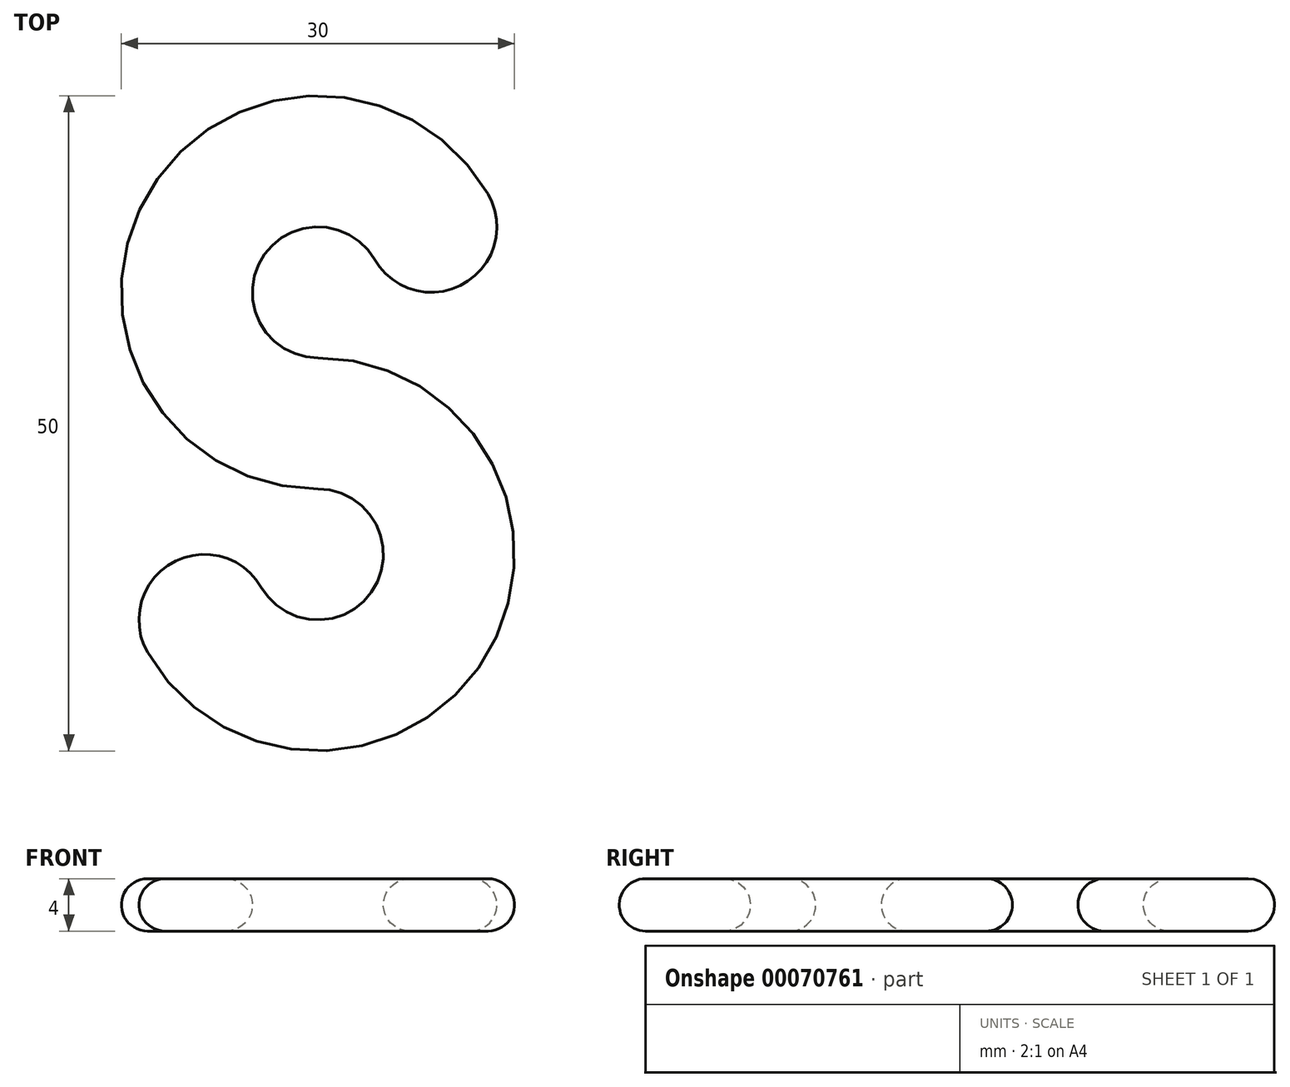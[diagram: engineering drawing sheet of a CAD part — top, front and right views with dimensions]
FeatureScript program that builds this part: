
annotation { "Feature Type Name" : "Feature", "Feature Type Description" : "" }
export const myFeature = defineFeature(function(context is Context, id is Id, definition is map)
    precondition{}
    {
        {
            var Q0;
            Q0=qCreatedBy(makeId("Top.planeOp"),FACE);
            var sketch = newSketch(context, id + "F0", { "sketchPlane" : qUnion([Q0])});
            skCircle(sketch, "E0", {"center": v(0, 0) * mm, "radius": 15 * mm});
            skCircle(sketch, "E1", {"center": v(0, 0) * mm, "radius": 5 * mm});
            skCircle(sketch, "E2", {"center": v(-8.66, -5) * mm, "radius": 5 * mm});
            skCircle(sketch, "E3", {"center": v(0, 20) * mm, "radius": 15 * mm});
            skCircle(sketch, "E4", {"center": v(0, 20) * mm, "radius": 5 * mm});
            skCircle(sketch, "E5", {"center": v(8.66, 25) * mm, "radius": 5 * mm});
            skSolve(sketch);
        }
        {
            var Q0;
            {var subQ0=sQuery(id+"F0.wireOp",EDGE,"E3");var subQ1=sQuery(id+"F0.wireOp",EDGE,"E0");var subQ2=makeQuery(id+"F0.imprint","INTERSECT",VERTEX,{"disambiguationData":[OD(1.0)],"derivedFrom":[subQ1,subQ0]});Q0=makeQuery(id+"F0.imprint","IMPRINT",FACE,{"disambiguationData":[TD([[makeQuery(id+"F0.imprint","IMPRINT",EDGE,{"disambiguationData":[TD([[subQ2,1.0]])],"derivedFrom":subQ1}),-1.0]])]});}
            var Q1;
            {var subQ0=sQuery(id+"F0.wireOp",EDGE,"E5");var subQ1=makeQuery(id+"F0.imprint","INTERSECT",VERTEX,{"derivedFrom":[sQuery(id+"F0.wireOp",EDGE,"E3"),subQ0]});Q1=makeQuery(id+"F0.imprint","IMPRINT",FACE,{"disambiguationData":[TD([[makeQuery(id+"F0.imprint","IMPRINT",EDGE,{"disambiguationData":[TD([[subQ1,-1.0]])],"derivedFrom":subQ0}),1.0]])]});}
            var Q2;
            {var subQ0=sQuery(id+"F0.wireOp",EDGE,"E3");var subQ1=sQuery(id+"F0.wireOp",EDGE,"E0");var subQ2=makeQuery(id+"F0.imprint","INTERSECT",VERTEX,{"disambiguationData":[OD(0.0)],"derivedFrom":[subQ1,subQ0]});Q2=makeQuery(id+"F0.imprint","IMPRINT",FACE,{"disambiguationData":[TD([[makeQuery(id+"F0.imprint","IMPRINT",EDGE,{"disambiguationData":[TD([[subQ2,-1.0]])],"derivedFrom":subQ1}),1.0]])]});}
            var Q3;
            {var subQ0=sQuery(id+"F0.wireOp",EDGE,"E3");var subQ1=sQuery(id+"F0.wireOp",EDGE,"E0");var subQ2=makeQuery(id+"F0.imprint","INTERSECT",VERTEX,{"disambiguationData":[OD(0.0)],"derivedFrom":[subQ1,subQ0]});Q3=makeQuery(id+"F0.imprint","IMPRINT",FACE,{"disambiguationData":[TD([[makeQuery(id+"F0.imprint","IMPRINT",EDGE,{"disambiguationData":[TD([[subQ2,1.0]])],"derivedFrom":subQ1}),1.0]])]});}
            var Q4;
            {var subQ0=sQuery(id+"F0.wireOp",EDGE,"E2");var subQ1=makeQuery(id+"F0.imprint","INTERSECT",VERTEX,{"derivedFrom":[sQuery(id+"F0.wireOp",EDGE,"E0"),subQ0]});Q4=makeQuery(id+"F0.imprint","IMPRINT",FACE,{"disambiguationData":[TD([[makeQuery(id+"F0.imprint","IMPRINT",EDGE,{"disambiguationData":[TD([[subQ1,1.0]])],"derivedFrom":subQ0}),1.0]])]});}
            extrude(context, id + "F1", {"entities" : qUnion([Q0, Q1, Q2, Q3, Q4]), "depth" : 4 * mm});
        }
        {
            var Q0;
            Q0=makeQuery(id+"F1.opExtrude","CAP_FACE",FACE,{"disambiguationData":[OSD([sQuery(id+"F0.wireOp",EDGE,"E0"),sQuery(id+"F0.wireOp",EDGE,"E1"),sQuery(id+"F0.wireOp",EDGE,"E2"),sQuery(id+"F0.wireOp",EDGE,"E3"),sQuery(id+"F0.wireOp",EDGE,"E4"),sQuery(id+"F0.wireOp",EDGE,"E5")])],"isStart":false});
            var Q1;
            Q1=makeQuery(id+"F1.opExtrude","CAP_FACE",FACE,{"disambiguationData":[OSD([sQuery(id+"F0.wireOp",EDGE,"E0"),sQuery(id+"F0.wireOp",EDGE,"E1"),sQuery(id+"F0.wireOp",EDGE,"E2"),sQuery(id+"F0.wireOp",EDGE,"E3"),sQuery(id+"F0.wireOp",EDGE,"E4"),sQuery(id+"F0.wireOp",EDGE,"E5")])],"isStart":true});
            fillet(context, id + "F2", {"entities" : qUnion([Q0, Q1]), "radius" : 2 * mm, "tangentPropagation" : true, "allowEdgeOverflow" : false});
        }
    });
